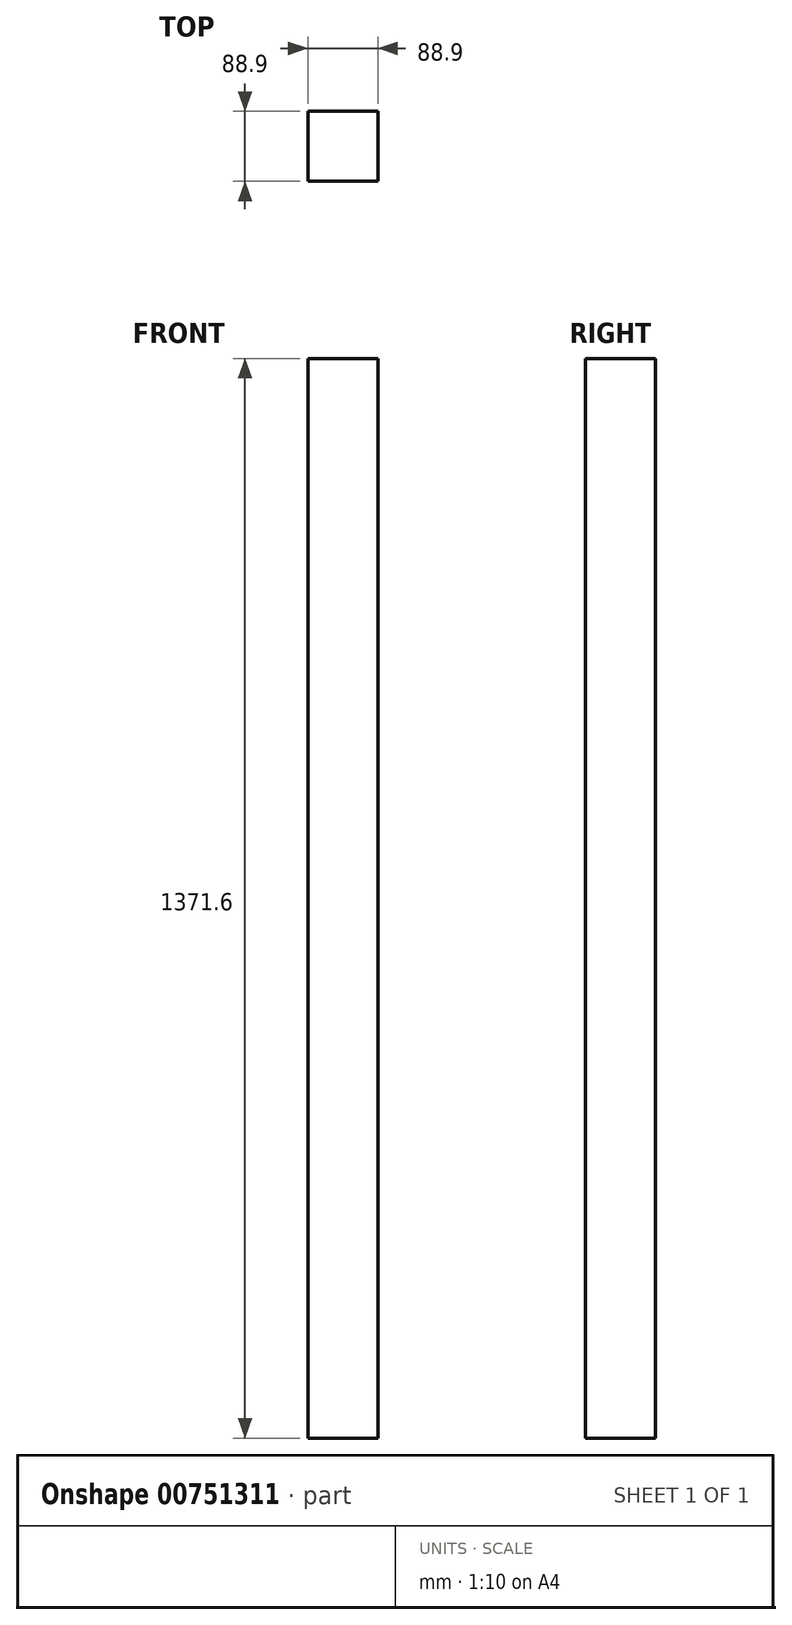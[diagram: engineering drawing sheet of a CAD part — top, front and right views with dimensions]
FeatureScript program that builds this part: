
annotation { "Feature Type Name" : "Feature", "Feature Type Description" : "" }
export const myFeature = defineFeature(function(context is Context, id is Id, definition is map)
    precondition{}
    {
        {
            var Q0;
            Q0=qCreatedBy(makeId("Top.planeOp"),FACE);
            var sketch = newSketch(context, id + "F0", { "sketchPlane" : qUnion([Q0])});
            skLineSegment(sketch, "E0.bottom", {"start": v(0, 0) * mm, "end": v(88.9, 0) * mm});
            skLineSegment(sketch, "E0.top", {"start": v(0, 88.9) * mm, "end": v(88.9, 88.9) * mm});
            skLineSegment(sketch, "E0.left", {"start": v(0, 0) * mm, "end": v(0, 88.9) * mm});
            skLineSegment(sketch, "E0.right", {"start": v(88.9, 0) * mm, "end": v(88.9, 88.9) * mm});
            skSolve(sketch);
        }
        {
            var Q0;
            Q0 = qSketchRegion(id + "F0", true);
            extrude(context, id + "F1", {"entities" : qUnion([Q0]), "depth" : 1371.6 * mm, "offsetDistance" : 25.4 * mm});
        }
    });
